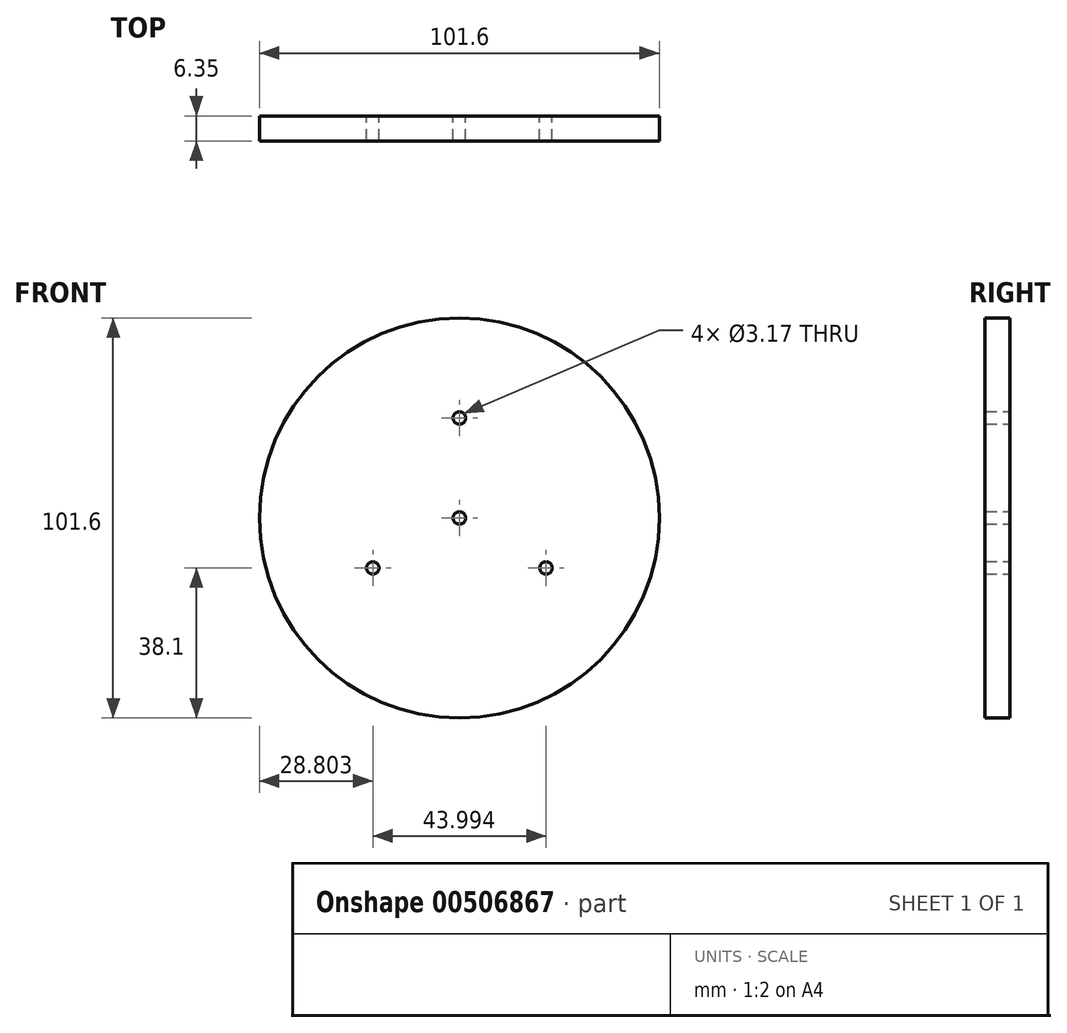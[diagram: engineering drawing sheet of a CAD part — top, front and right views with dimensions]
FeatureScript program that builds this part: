
annotation { "Feature Type Name" : "Feature", "Feature Type Description" : "" }
export const myFeature = defineFeature(function(context is Context, id is Id, definition is map)
    precondition{}
    {
        {
            var Q0;
            Q0=qCreatedBy(makeId("Front.planeOp"),FACE);
            var sketch = newSketch(context, id + "F0", { "sketchPlane" : qUnion([Q0])});
            skCircle(sketch, "E0", {"center": v(0, 0) * mm, "radius": 50.8 * mm});
            skPoint(sketch, "E1", {"position": v(0, 25.4) * mm});
            skPoint(sketch, "E2", {"position": v(-22, -12.7) * mm});
            skPoint(sketch, "E3", {"position": v(22, -12.7) * mm});
            skLineSegment(sketch, "E4", {"start": v(0, 0) * mm, "end": v(0, 25.4) * mm, "construction": true});
            skLineSegment(sketch, "E5", {"start": v(22, -12.7) * mm, "end": v(0, 0) * mm, "construction": true});
            skLineSegment(sketch, "E6", {"start": v(-22, -12.7) * mm, "end": v(0, 0) * mm, "construction": true});
            skSolve(sketch);
        }
        {
            var Q0;
            Q0 = qSketchRegion(id + "F0", true);
            extrude(context, id + "F1", {"entities" : qUnion([Q0]), "depth" : 6.35 * mm, "offsetDistance" : 25.4 * mm});
        }
        {
            var Q0;
            Q0=sQuery(id+"F0.wireOp",VERTEX,"E0.center");
            var Q1;
            Q1=makeQuery(id+"F1.opExtrude","SWEPT_BODY",BODY,{"disambiguationData":[OSD([sQuery(id+"F0.wireOp",EDGE,"E0")])]});
            hole(context, id + "F2", {"style" : HoleStyle.SIMPLE, "endStyle" : HoleEndStyle.THROUGH, "oppositeDirection" : true, "holeDiameter" : 3.17 * mm, "isTappedThrough" : true, "tappedDepth" : 12.7 * mm, "tapClearance" : 3, "locations" : qUnion([Q0]), "scope" : qUnion([Q1])});
        }
        {
            var Q0;
            Q0=sQuery(id+"F0.wireOp",VERTEX,"E1");
            var Q1;
            Q1=sQuery(id+"F0.wireOp",VERTEX,"E3");
            var Q2;
            Q2=sQuery(id+"F0.wireOp",VERTEX,"E2");
            var Q3;
            Q3=makeQuery(id+"F1.opExtrude","SWEPT_BODY",BODY,{"disambiguationData":[OSD([sQuery(id+"F0.wireOp",EDGE,"E0")])]});
            hole(context, id + "F3", {"style" : HoleStyle.SIMPLE, "endStyle" : HoleEndStyle.THROUGH, "oppositeDirection" : true, "holeDiameter" : 3.17 * mm, "isTappedThrough" : true, "tappedDepth" : 12.7 * mm, "tapClearance" : 3, "locations" : qUnion([Q0, Q1, Q2]), "scope" : qUnion([Q3])});
        }
    });
